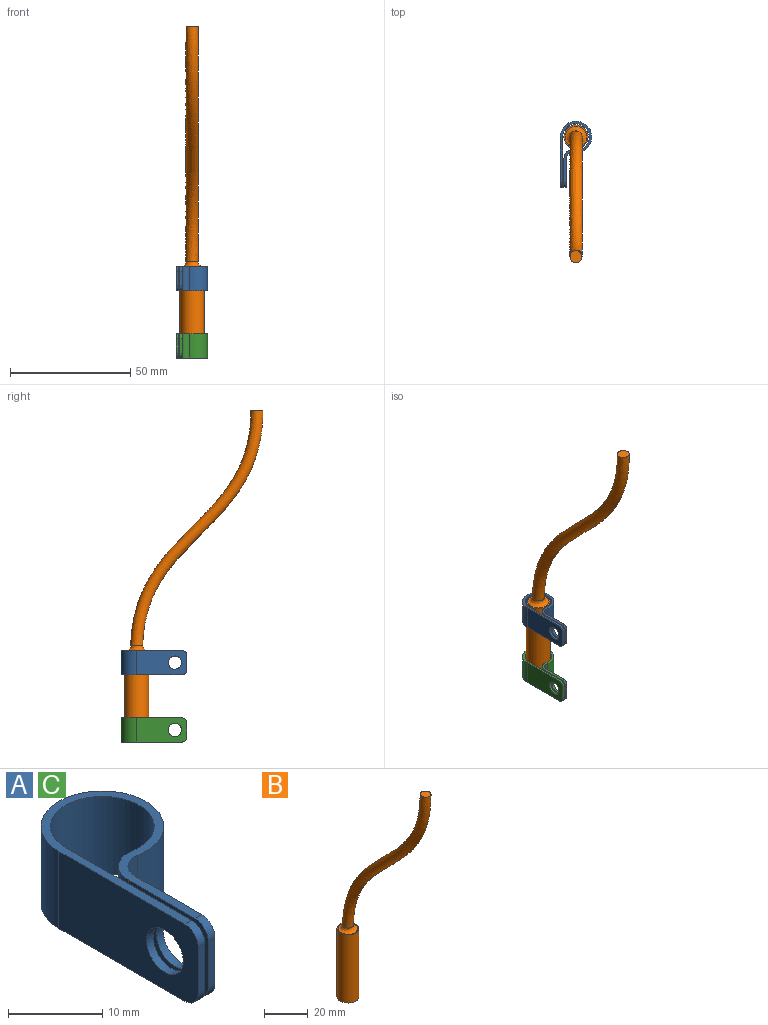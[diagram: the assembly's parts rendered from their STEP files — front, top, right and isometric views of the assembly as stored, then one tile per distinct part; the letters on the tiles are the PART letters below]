
ASSEMBLY  parts=3 mates=2
PART A: 18 faces, bbox 13x27.4x10 mm
  f0: cylinder r=2.5mm len=10mm, axis (0,0,-1), area 43.5mm2, adj f1,f9,f10,f11
  f1: cylinder r=6.5mm len=13mm, axis (0,0,-1), area 317.2mm2, adj f0,f2,f10,f11
  f2: plane 20.87x10mm, normal (-1,0,0), area 183.3mm2, adj f1,f3,f10,f11,f13,f15,f17
  f3: plane 6x1mm, normal (0,-1,0), area 6mm2, adj f2,f4,f15,f17
  f4: plane 20.87x10mm, normal (1,0,0), area 183.3mm2, adj f3,f5,f10,f11,f13,f15,f17
  f5: cylinder r=5.5mm len=11mm, axis (0,0,-1), area 268.4mm2, adj f4,f6,f10,f11
  f6: cylinder r=3.5mm len=10mm, axis (0,0,-1), area 60.8mm2, adj f5,f7,f10,f11
  f7: plane 12x10mm, normal (-1,0,0), area 94.5mm2, adj f6,f8,f10,f11,f12,f14,f16
  f8: plane 6x1mm, normal (0,-1,0), area 6mm2, adj f7,f9,f14,f16
  f9: plane 12x10mm, normal (1,0,0), area 94.5mm2, adj f0,f8,f10,f11,f12,f14,f16
  f10: plane 25.37x13mm, normal (0,0,1), area 63.4mm2, adj f0,f1,f2,f4,f5,f6,f7,f9
  f11: plane 25.37x13mm, normal (0,0,-1), area 63.4mm2, adj f0,f1,f2,f4,f5,f6,f7,f9
  f12: cylinder r=2.75mm len=5.5mm, axis (1,0,0), area 17.3mm2, adj f7,f9
  f13: cylinder r=2.75mm len=5.5mm, axis (1,0,0), area 17.3mm2, adj f2,f4
  f14: cylinder r=2mm len=2mm, axis (1,0,0), area 3.1mm2, adj f7,f8,f9,f11
  f15: cylinder r=2mm len=2mm, axis (1,0,0), area 3.1mm2, adj f2,f3,f4,f11
  f16: cylinder r=2mm len=2mm, axis (-1,0,0), area 3.1mm2, adj f7,f8,f9,f10
  f17: cylinder r=2mm len=2mm, axis (-1,0,0), area 3.1mm2, adj f2,f3,f4,f10
PART B: 6 faces, bbox 10x57.5x138 mm
  f0: cylinder r=5mm len=38mm, axis (0,0,-1), area 1193.8mm2, adj f1,f2
  f1: plane 10x10mm, normal (0,0,1), area 14.9mm2, adj f0,f5
  f2: plane 10x10mm, normal (0,0,-1), area 78.5mm2, adj f0
  f3: plane 5x5mm, normal (0,0,1), area 19.6mm2, adj f4
  f4: bspline ~98.18x54.93mm, area 1783.1mm2, adj f3,f5
  f5: bspline ~9.01x9mm, area 63.7mm2, adj f1,f4
PART C: same geometry as A
PLACE A t=(0,0,28)mm
PLACE B at identity
PLACE C at identity
MATE fastened B.f0 <-> C.f1  axis (0,0,-1) through (0,0,0)mm
MATE fastened B.f0 <-> A.f1  axis (0,0,1) through (0,0,38)mm
